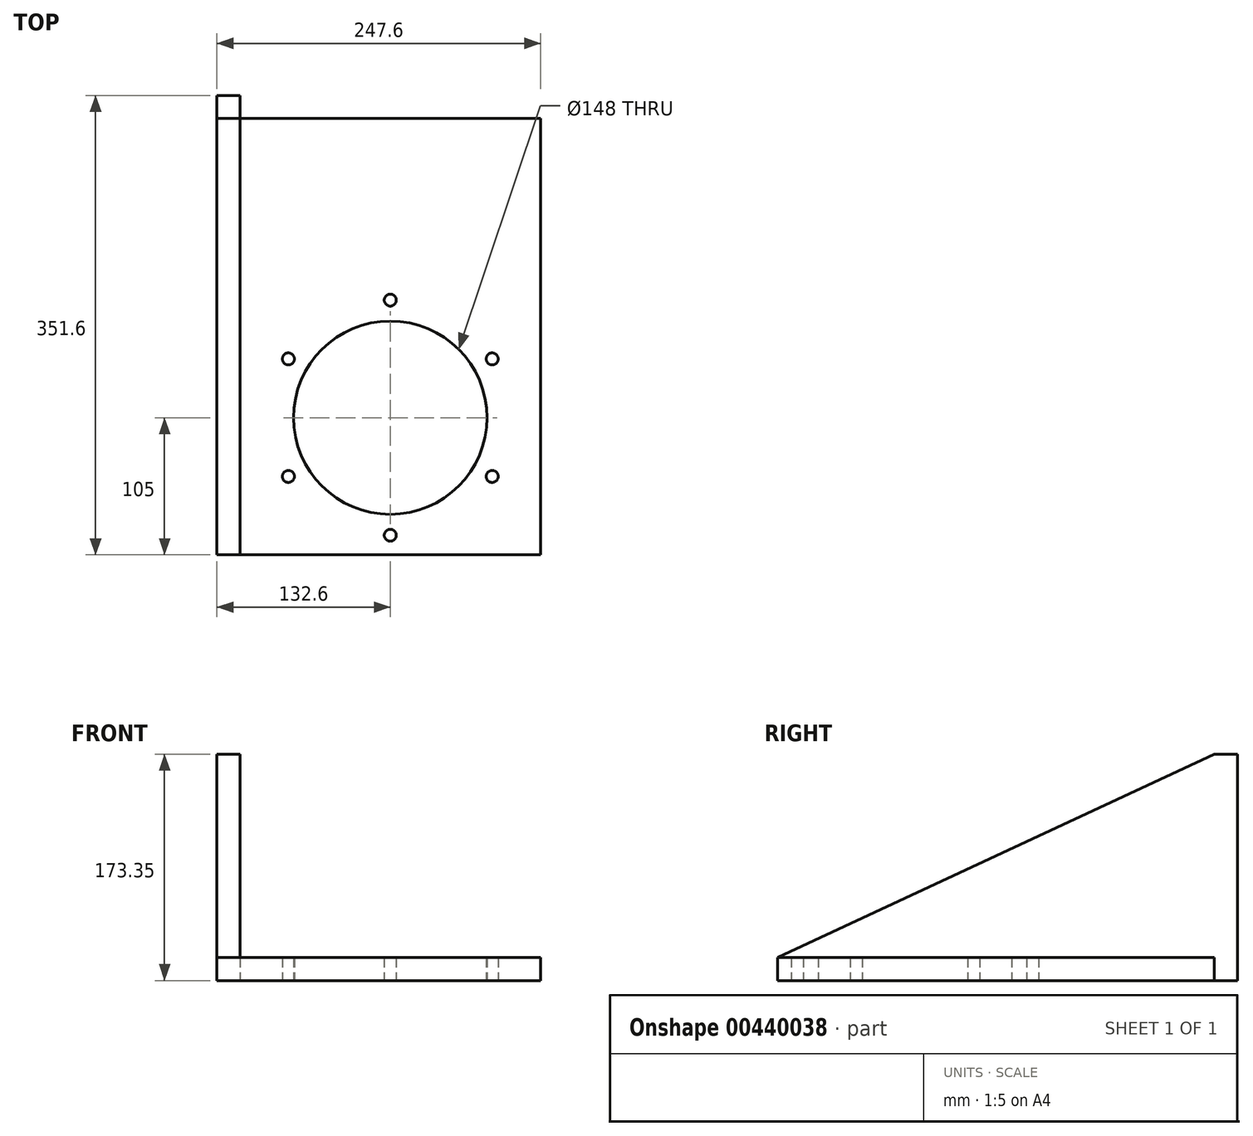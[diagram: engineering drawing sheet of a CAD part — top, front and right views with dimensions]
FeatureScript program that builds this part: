
annotation { "Feature Type Name" : "Feature", "Feature Type Description" : "" }
export const myFeature = defineFeature(function(context is Context, id is Id, definition is map)
    precondition{}
    {
        {
            assignVariable(context, id + "F0", {"name" : "PlyThick", "anyValue" : 17.6});
        }
        {
            var Q0;
            Q0=qCreatedBy(makeId("Top.planeOp"),FACE);
            var sketch = newSketch(context, id + "F1", { "sketchPlane" : qUnion([Q0])});
            skCircle(sketch, "E0", {"center": v(0, 0) * mm, "radius": 74 * mm});
            skCircle(sketch, "E1", {"center": v(0, 90) * mm, "radius": 4.6 * mm});
            skCircle(sketch, "E2.1.0", {"center": v(-77.94, 45) * mm, "radius": 4.6 * mm});
            skCircle(sketch, "E2.2.0", {"center": v(-77.94, -45) * mm, "radius": 4.6 * mm});
            skCircle(sketch, "E2.3.0", {"center": v(0, -90) * mm, "radius": 4.6 * mm});
            skCircle(sketch, "E2.4.0", {"center": v(77.94, -45) * mm, "radius": 4.6 * mm});
            skCircle(sketch, "E2.5.0", {"center": v(77.94, 45) * mm, "radius": 4.6 * mm});
            skLineSegment(sketch, "E3.bottom", {"start": v(-115, 229) * mm, "end": v(115, 229) * mm});
            skLineSegment(sketch, "E3.top", {"start": v(-115, -105) * mm, "end": v(115, -105) * mm});
            skLineSegment(sketch, "E3.left", {"start": v(-115, 229) * mm, "end": v(-115, -105) * mm});
            skLineSegment(sketch, "E3.right", {"start": v(115, 229) * mm, "end": v(115, -105) * mm});
            skLineSegment(sketch, "E4", {"start": v(0, 0) * mm, "end": v(0, -105) * mm, "construction": true});
            skLineSegment(sketch, "E5", {"start": v(0, 90) * mm, "end": v(0, 0) * mm, "construction": true});
            skCircle(sketch, "E6", {"center": v(0, 0) * mm, "radius": 105 * mm});
            skCircle(sketch, "E7", {"center": v(0, 0) * mm, "radius": 189 * mm});
            skLineSegment(sketch, "E8", {"start": v(115, 0) * mm, "end": v(105, 0) * mm, "construction": true});
            skLineSegment(sketch, "E9", {"start": v(0, 189) * mm, "end": v(0, 229) * mm, "construction": true});
            skSolve(sketch);
        }
        {
            var Q0;
            {var subQ7=sQuery(id+"F1.wireOp",EDGE,"E6");Q0=makeQuery(id+"F1.imprint","IMPRINT",FACE,{"disambiguationData":[TD([[makeQuery(id+"F1.imprint","IMPRINT",EDGE,{"derivedFrom":subQ7}),-1.0]])]});}
            var Q1;
            {var subQ0=sQuery(id+"F1.wireOp",EDGE,"E3.bottom");Q1=makeQuery(id+"F1.imprint","IMPRINT",FACE,{"disambiguationData":[TD([[makeQuery(id+"F1.imprint","IMPRINT",EDGE,{"derivedFrom":subQ0}),-1.0]])]});}
            var Q2;
            Q2=makeQuery(id+"F1.imprint","IMPRINT",FACE,{"disambiguationData":[TD([[makeQuery(id+"F1.imprint","IMPRINT",EDGE,{"derivedFrom":sQuery(id+"F1.wireOp",EDGE,"E0")}),-1.0]])]});
            extrude(context, id + "F2", {"entities" : qUnion([Q0, Q1, Q2]), "depth" : (getVariable(context, 'PlyThick')) * mm});
        }
        {
            var Q0;
            Q0=makeQuery(id+"F2.opExtrude","SWEPT_FACE",FACE,{"disambiguationData":[OSD([sQuery(id+"F1.wireOp",EDGE,"E3.left")])]});
            var sketch = newSketch(context, id + "F3", { "sketchPlane" : qUnion([Q0])});
            skLineSegment(sketch, "E10", {"start": v(105, 0) * mm, "end": v(105, 17.6) * mm});
            skLineSegment(sketch, "E11", {"start": v(105, 17.6) * mm, "end": v(-229, 173.35) * mm});
            skLineSegment(sketch, "E12", {"start": v(-229, 173.35) * mm, "end": v(-246.6, 173.35) * mm});
            skLineSegment(sketch, "E13", {"start": v(-246.6, 173.35) * mm, "end": v(-246.6, 0) * mm});
            skLineSegment(sketch, "E14", {"start": v(-246.6, 0) * mm, "end": v(105, 0) * mm});
            skSolve(sketch);
        }
        {
            var Q0;
            Q0=makeQuery(id+"F3.imprint","IMPRINT",FACE,{"disambiguationData":[TD([[makeQuery(id+"F3.imprint","IMPRINT",EDGE,{"derivedFrom":sQuery(id+"F3.wireOp",EDGE,"E11")}),1.0]])]});
            var Q1;
            {var subQ0=sQuery(id+"F3.wireOp",EDGE,"E10");Q1=makeQuery(id+"F3.imprint","IMPRINT",FACE,{"disambiguationData":[TD([[makeQuery(id+"F3.imprint","IMPRINT",EDGE,{"derivedFrom":subQ0}),-1.0]])]});}
            extrude(context, id + "F4", {"entities" : qUnion([Q0, Q1]), "operationType" : NewBodyOperationType.ADD, "depth" : (getVariable(context, 'PlyThick')) * mm});
        }
    });
